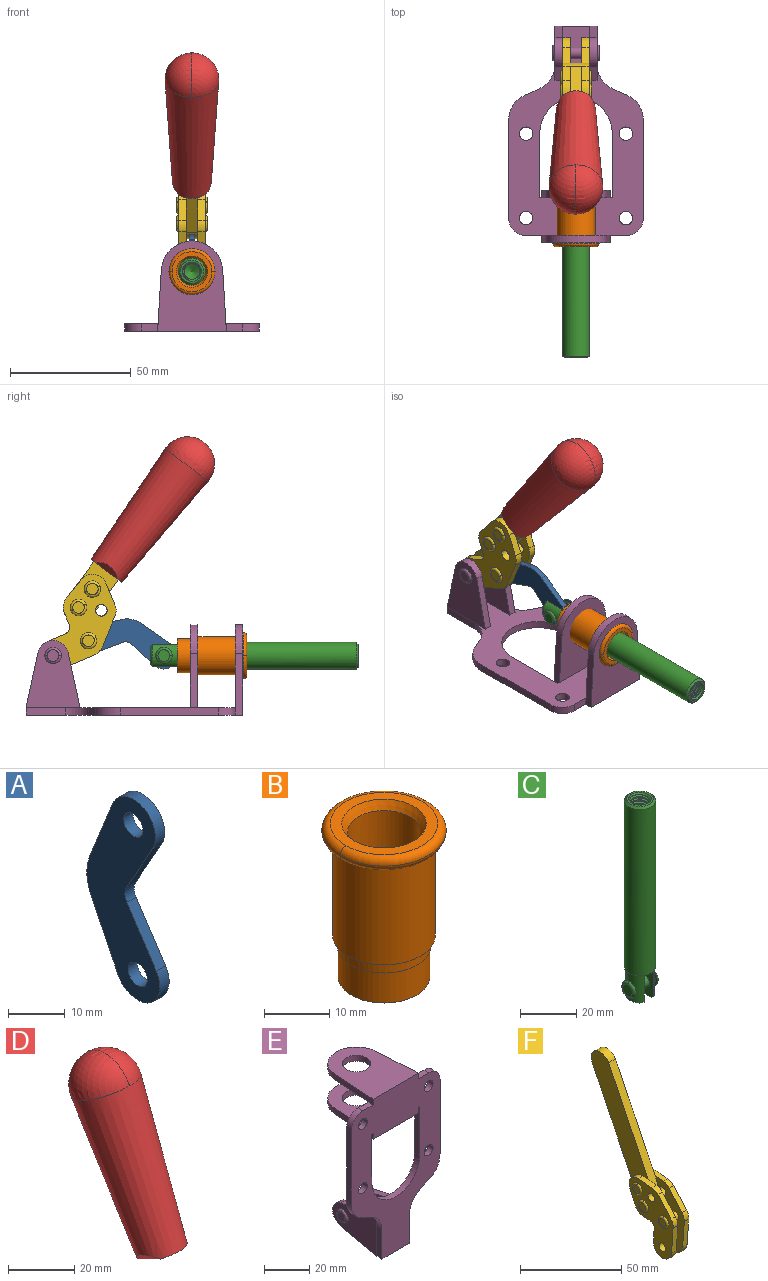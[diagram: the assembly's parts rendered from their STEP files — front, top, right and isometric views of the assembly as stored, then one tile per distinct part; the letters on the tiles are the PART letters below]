
ASSEMBLY  parts=6 mates=6
PART A: 12 faces, bbox 2.3x18.2x42.8 mm
  f0: cylinder r=2.4mm len=4.8mm, axis (1,0,0), area 34.9mm2, adj f4,f11
  f1: cylinder r=10.41mm len=8.47mm, axis (1,0,0), area 20.2mm2, adj f4,f9,f10,f11
  f2: cylinder r=3.05mm len=3.16mm, axis (1,0,0), area 7.7mm2, adj f4,f6,f7,f11
  f3: cylinder r=2.4mm len=4.8mm, axis (1,0,0), area 34.9mm2, adj f4,f11
  f4: plane 42.81x18.23mm, normal (-1,0,0), area 414.1mm2, adj f0,f1,f2,f3,f5,f6,f7,f8
  f5: cylinder r=5.54mm len=10.67mm, axis (1,0,0), area 41.8mm2, adj f4,f6,f10,f11
  f6: plane 11.66x6.53mm, normal (0,-0.87,-0.49), area 30.9mm2, adj f2,f4,f5,f11
  f7: plane 11.17x7.33mm, normal (0,-0.84,0.55), area 30.9mm2, adj f2,f4,f8,f11
  f8: cylinder r=5.54mm len=10.51mm, axis (1,0,0), area 41.8mm2, adj f4,f7,f9,f11
  f9: plane 13.67x6.67mm, normal (0,0.9,-0.44), area 35.1mm2, adj f1,f4,f8,f11
  f10: plane 14.1x5.7mm, normal (0,0.93,0.37), area 35.1mm2, adj f1,f4,f5,f11
  f11: plane 42.81x18.23mm, normal (1,0,0), area 414.1mm2, adj f0,f1,f2,f3,f5,f6,f7,f8
PART B: 15 faces, bbox 20.6x20.6x28.7 mm
  f0: torus R=8.26mm, axis (0,0,1), area 56.8mm2, adj f1,f10,f12
  f1: torus R=8.26mm, axis (0,0,1), area 56.8mm2, adj f0,f6,f13
  f2: cylinder r=5.59mm len=25.91mm, axis (0,0,1), area 909.6mm2, adj f3,f4
  f3: cone r=6.86mm half-angle=45deg, axis (0,0,-1), area 70.2mm2, adj f2,f14
  f4: cone r=6.47mm half-angle=30deg, axis (0,0,1), area 66.7mm2, adj f2,f13
  f5: cylinder r=7.04mm len=14.07mm, axis (0,0,1), area 252.6mm2, adj f11,f14
  f6: torus R=8.26mm, axis (0,0,1), area 56.8mm2, adj f1,f12,f13
  f7: cylinder r=7.16mm len=14.33mm, axis (0,0,1), area 91.5mm2, adj f9,f11
  f8: cylinder r=7.86mm len=18.42mm, axis (0,0,1), area 909.6mm2, adj f9,f10
  f9: plane 15.72x15.72mm, normal (0,0,-1), area 33mm2, adj f7,f8
  f10: plane 16.51x16.51mm, normal (0,0,-1), area 19.9mm2, adj f0,f8,f12
  f11: plane 14.33x14.33mm, normal (0,0,-1), area 5.7mm2, adj f5,f7
  f12: torus R=8.26mm, axis (0,0,1), area 56.8mm2, adj f0,f6,f10
  f13: plane 16.51x16.51mm, normal (0,0,1), area 82.7mm2, adj f1,f4,f6
  f14: plane 14.07x14.07mm, normal (0,0,-1), area 7.8mm2, adj f3,f5
PART C: 48 faces, bbox 12.6x11.1x86.1 mm
  f0: torus R=2.41mm, axis (-1,0,0), area 15mm2, adj f30,f32,f34
  f1: torus R=2.41mm, axis (-1,0,0), area 15mm2, adj f29,f31,f33
  f2: cylinder r=5.54mm len=72.39mm, axis (0,0,1), area 2518.5mm2, adj f3,f4,f42,f43
  f3: cone r=5.54mm half-angle=45deg, axis (0,0,1), area 7.6mm2, adj f2,f5,f41
  f4: cone r=5.54mm half-angle=45deg, axis (0,0,-1), area 34.9mm2, adj f2,f39
  f5: cylinder r=5.08mm len=11.48mm, axis (0,0,1), area 108.3mm2, adj f3,f7,f8,f41
  f6: cylinder r=2.41mm len=4.83mm, axis (-1,0,0), area 71.2mm2, adj f40,f41
  f7: cylinder r=2.41mm len=4.83mm, axis (-1,0,0), area 7.6mm2, adj f5,f34
  f8: cone r=5.08mm half-angle=45deg, axis (0,0,1), area 10.6mm2, adj f5,f37,f41
  f9: cone r=3.98mm half-angle=45deg, axis (0,0,1), area 17.6mm2, adj f27,f39,f45,f46,f47
  f10: cylinder r=2.41mm len=4.83mm, axis (-1,0,0), area 7.6mm2, adj f33,f38
  f11: cylinder r=3.2mm len=6.4mm, axis (0,0,1), area 78.4mm2, adj f12,f28,f44,f45,f47
  f12: cylinder r=3.2mm len=6.4mm, axis (0,0,1), area 10.5mm2, adj f11,f13,f45,f47
  f13: cylinder r=3.2mm len=6.4mm, axis (0,0,1), area 10.5mm2, adj f12,f14,f45,f47
  f14: cylinder r=3.2mm len=6.4mm, axis (0,0,1), area 10.5mm2, adj f13,f15,f45,f47
  f15: cylinder r=3.2mm len=6.4mm, axis (0,0,1), area 10.5mm2, adj f14,f16,f45,f47
  f16: cylinder r=3.2mm len=6.4mm, axis (0,0,1), area 10.5mm2, adj f15,f17,f45,f47
  f17: cylinder r=3.2mm len=6.4mm, axis (0,0,1), area 10.5mm2, adj f16,f18,f45,f47
  f18: cylinder r=3.2mm len=6.4mm, axis (0,0,1), area 10.5mm2, adj f17,f19,f45,f47
  f19: cylinder r=3.2mm len=6.4mm, axis (0,0,1), area 10.5mm2, adj f18,f20,f45,f47
  f20: cylinder r=3.2mm len=6.4mm, axis (0,0,1), area 10.5mm2, adj f19,f21,f45,f47
  f21: cylinder r=3.2mm len=6.4mm, axis (0,0,1), area 10.5mm2, adj f20,f22,f45,f47
  f22: cylinder r=3.2mm len=6.4mm, axis (0,0,1), area 10.5mm2, adj f21,f23,f45,f47
  f23: cylinder r=3.2mm len=6.4mm, axis (0,0,1), area 10.5mm2, adj f22,f24,f45,f47
  f24: cylinder r=3.2mm len=6.4mm, axis (0,0,1), area 10.5mm2, adj f23,f25,f45,f47
  f25: cylinder r=3.2mm len=6.4mm, axis (0,0,1), area 10.5mm2, adj f24,f26,f45,f47
  f26: cylinder r=3.2mm len=6.4mm, axis (0,0,1), area 10.5mm2, adj f25,f27,f45,f47
  f27: cylinder r=3.2mm len=6.4mm, axis (0,0,1), area 7.4mm2, adj f9,f26,f45,f47
  f28: cone r=3.2mm half-angle=60deg, axis (0,0,1), area 37.2mm2, adj f11
  f29: plane 4.83x4.83mm, normal (-1,0,0), area 18.3mm2, adj f1,f31
  f30: plane 4.83x4.83mm, normal (1,0,0), area 18.3mm2, adj f0,f32
  f31: torus R=2.41mm, axis (-1,0,0), area 15mm2, adj f1,f29,f33
  f32: torus R=2.41mm, axis (-1,0,0), area 15mm2, adj f0,f30,f34
  f33: plane 6.83x6.83mm, normal (1,0,0), area 18.3mm2, adj f1,f10,f31
  f34: plane 6.83x6.83mm, normal (-1,0,0), area 18.3mm2, adj f0,f7,f32
  f35: cone r=5.08mm half-angle=45deg, axis (0,0,1), area 10.6mm2, adj f36,f38,f40
  f36: plane 7.25x1.97mm, normal (0,0,-1), area 10mm2, adj f35,f40
  f37: plane 7.25x1.97mm, normal (0,0,-1), area 10mm2, adj f8,f41
  f38: cylinder r=5.08mm len=11.48mm, axis (0,0,1), area 108.3mm2, adj f10,f35,f40,f42
  f39: plane 9.55x9.55mm, normal (0,0,1), area 22mm2, adj f4,f9
  f40: plane 12.76x10.09mm, normal (1,0,0), area 95.7mm2, adj f6,f35,f36,f38,f42,f43
  f41: plane 12.76x10.09mm, normal (-1,0,0), area 95.7mm2, adj f3,f5,f6,f8,f37,f43
  f42: cone r=5.54mm half-angle=45deg, axis (0,0,1), area 7.6mm2, adj f2,f38,f40
  f43: plane 11.07x4.7mm, normal (0,0,-1), area 50.4mm2, adj f2,f40,f41
  f44: plane 0.89x0.62mm, normal (-1,0,0), area 0.3mm2, adj f11,f45,f46,f47
  f45: bspline ~24.8x7.63mm, area 266.6mm2, adj f9,f11,f12,f13,f14,f15,f16,f17
  f46: bspline ~24.87x7.63mm, area 73.6mm2, adj f9,f44,f45,f47
  f47: bspline ~24.98x7.63mm, area 272.5mm2, adj f9,f11,f12,f13,f14,f15,f16,f17
PART D: 11 faces, bbox 22.3x42.6x64.5 mm
  f0: sphere r=11.13mm, area 411.4mm2, adj f1,f8
  f1: cone r=11.11mm half-angle=3.3deg, axis (0,0.44,0.9), area 3251.8mm2, adj f0,f7,f8,f9,f10
  f2: cylinder r=6.16mm len=11.7mm, axis (1,0,0), area 89.5mm2, adj f3,f4,f5,f6
  f3: plane 60.23x36.75mm, normal (-1,0,0), area 763.6mm2, adj f2,f4,f6,f10
  f4: plane 51.37x25.05mm, normal (0,0.9,-0.44), area 264.2mm2, adj f2,f3,f5,f10
  f5: plane 60.23x36.75mm, normal (1,0,0), area 763.6mm2, adj f2,f4,f6,f10
  f6: plane 51.37x25.05mm, normal (0,-0.9,0.44), area 264.2mm2, adj f2,f3,f5,f10
  f7: plane 9.95x5.95mm, normal (0.71,-0.31,-0.64), area 25.8mm2, adj f1,f10
  f8: sphere r=11.13mm, area 411.4mm2, adj f0,f1
  f9: plane 9.95x5.95mm, normal (-0.71,-0.31,-0.64), area 25.8mm2, adj f1,f10
  f10: plane 14.27x11.38mm, normal (0,-0.44,-0.9), area 106.7mm2, adj f1,f3,f4,f5,f6,f7,f9
PART E: 55 faces, bbox 55.7x37.4x89.8 mm
  f0: torus R=2.41mm, axis (-1,0,0), area 15mm2, adj f11,f15,f25
  f1: torus R=2.41mm, axis (-1,0,0), area 15mm2, adj f10,f12,f22
  f2: cylinder r=2.78mm len=5.56mm, axis (0,-1,0), area 54.2mm2, adj f30,f54
  f3: cylinder r=14.99mm len=29.97mm, axis (0,-1,0), area 145.9mm2, adj f30,f49,f53,f54
  f4: cylinder r=2.78mm len=5.56mm, axis (0,-1,0), area 54.2mm2, adj f30,f54
  f5: cylinder r=2.78mm len=5.56mm, axis (0,-1,0), area 54.2mm2, adj f30,f54
  f6: cylinder r=2.78mm len=5.56mm, axis (0,-1,0), area 54.2mm2, adj f30,f54
  f7: cylinder r=6.35mm len=12.7mm, axis (0,0,1), area 123.6mm2, adj f27,f51
  f8: cylinder r=6.35mm len=12.7mm, axis (0,0,-1), area 124.7mm2, adj f21,f35
  f9: cylinder r=2.41mm len=11.18mm, axis (-1,0,0), area 169.4mm2, adj f16,f19
  f10: plane 4.83x4.83mm, normal (1,0,0), area 18.3mm2, adj f1,f12
  f11: plane 4.83x4.83mm, normal (-1,0,0), area 18.3mm2, adj f0,f15
  f12: torus R=2.41mm, axis (-1,0,0), area 15mm2, adj f1,f10,f22
  f13: cylinder r=6.35mm len=12.41mm, axis (1,0,0), area 53.4mm2, adj f18,f19,f22,f23
  f14: cylinder r=6.35mm len=12.41mm, axis (-1,0,0), area 53.4mm2, adj f16,f17,f24,f25
  f15: torus R=2.41mm, axis (-1,0,0), area 15mm2, adj f0,f11,f25
  f16: plane 27.86x22.35mm, normal (1,0,0), area 425.4mm2, adj f9,f14,f17,f24,f30
  f17: plane 22.86x4.97mm, normal (0,0.21,0.98), area 72.5mm2, adj f14,f16,f25,f30
  f18: plane 22.86x4.97mm, normal (0,0.21,0.98), area 72.5mm2, adj f13,f19,f22,f30
  f19: plane 27.86x22.35mm, normal (-1,0,0), area 425.4mm2, adj f9,f13,f18,f23,f30
  f20: cylinder r=12.7mm len=25.35mm, axis (0,0,-1), area 119.8mm2, adj f21,f34,f35,f36
  f21: plane 34.21x28.07mm, normal (0,0,-1), area 702.4mm2, adj f8,f20,f30,f34,f36
  f22: plane 27.96x22.45mm, normal (1,0,0), area 407.2mm2, adj f1,f12,f13,f18,f23,f30,f42,f43
  f23: plane 22.86x4.97mm, normal (0,0.21,-0.98), area 72.5mm2, adj f13,f19,f22,f44
  f24: plane 22.86x4.97mm, normal (0,0.21,-0.98), area 72.5mm2, adj f14,f16,f25,f44
  f25: plane 27.86x22.35mm, normal (-1,0,0), area 407.1mm2, adj f0,f14,f15,f17,f24,f30,f45,f46
  f26: plane 3.1x0.95mm, normal (0,0,-1), area 2.7mm2, adj f30,f49,f50,f54
  f27: plane 34.21x28.07mm, normal (0,0,1), area 702.4mm2, adj f7,f28,f30,f50,f52
  f28: cylinder r=12.7mm len=25.35mm, axis (0,0,1), area 118.8mm2, adj f27,f50,f51,f52
  f29: plane 3.1x0.95mm, normal (0,0,-1), area 2.7mm2, adj f30,f52,f53,f54
  f30: plane 86.54x55.63mm, normal (0,1,0), area 2362.9mm2, adj f2,f3,f4,f5,f6,f16,f17,f18
  f31: plane 40.56x3.1mm, normal (-1,0,0), area 125.7mm2, adj f30,f32,f48,f54
  f32: cylinder r=7.11mm len=7.11mm, axis (0,-1,0), area 34.6mm2, adj f30,f31,f33,f54
  f33: plane 6.67x3.1mm, normal (0,0,1), area 20.4mm2, adj f30,f32,f34,f54
  f34: plane 25.39x3.13mm, normal (-1,0.06,0), area 79.5mm2, adj f20,f21,f33,f35,f54
  f35: plane 37.31x28.45mm, normal (0,0,1), area 789.9mm2, adj f8,f20,f34,f36,f54
  f36: plane 25.39x3.13mm, normal (1,0.06,0), area 79.5mm2, adj f20,f21,f35,f37,f54
  f37: plane 6.67x3.1mm, normal (0,0,1), area 20.4mm2, adj f30,f36,f38,f54
  f38: cylinder r=7.11mm len=7.11mm, axis (0,-1,0), area 34.6mm2, adj f30,f37,f39,f54
  f39: plane 40.56x3.1mm, normal (1,0,0), area 125.7mm2, adj f30,f38,f40,f54
  f40: cylinder r=11.18mm len=10.16mm, axis (0,-1,0), area 39.5mm2, adj f30,f39,f41,f54
  f41: plane 6.09x3.1mm, normal (0.42,0,-0.91), area 20.8mm2, adj f30,f40,f42,f54
  f42: cylinder r=11.18mm len=9.41mm, axis (0,-1,0), area 37.2mm2, adj f22,f30,f41,f43,f54
  f43: plane 16.5x3.1mm, normal (1,0,0), area 51.1mm2, adj f22,f42,f44,f54
  f44: plane 17.37x3.1mm, normal (0,0,-1), area 53.8mm2, adj f23,f24,f30,f43,f45,f54
  f45: plane 16.5x3.1mm, normal (-1,0,0), area 51.1mm2, adj f25,f44,f46,f54
  f46: cylinder r=11.18mm len=9.41mm, axis (0,-1,0), area 37.2mm2, adj f25,f30,f45,f47,f54
  f47: plane 6.09x3.1mm, normal (-0.42,0,-0.91), area 20.8mm2, adj f30,f46,f48,f54
  f48: cylinder r=11.18mm len=10.16mm, axis (0,-1,0), area 39.5mm2, adj f30,f31,f47,f54
  f49: plane 26.54x3.1mm, normal (-1,0,0), area 82.3mm2, adj f3,f26,f30,f54
  f50: plane 25.39x3.1mm, normal (1,0.06,0), area 78.8mm2, adj f26,f27,f28,f51,f54
  f51: plane 37.31x28.45mm, normal (0,0,-1), area 789.9mm2, adj f7,f28,f50,f52,f54
  f52: plane 25.39x3.1mm, normal (-1,0.06,0), area 78.8mm2, adj f27,f28,f29,f51,f54
  f53: plane 26.54x3.1mm, normal (1,0,0), area 82.3mm2, adj f3,f29,f30,f54
  f54: plane 89.66x55.63mm, normal (0,-1,0), area 2678.5mm2, adj f2,f3,f4,f5,f6,f26,f29,f31
PART F: 59 faces, bbox 12.9x60.2x99.6 mm
  f0: torus R=2.39mm, axis (-1,0,0), area 14.9mm2, adj f20,f43,f51
  f1: torus R=2.39mm, axis (-1,0,0), area 14.9mm2, adj f19,f42,f51
  f2: torus R=2.39mm, axis (-1,0,0), area 14.9mm2, adj f18,f35,f51
  f3: torus R=2.39mm, axis (-1,0,0), area 14.9mm2, adj f14,f17,f23
  f4: torus R=2.39mm, axis (-1,0,0), area 14.9mm2, adj f13,f16,f23
  f5: torus R=2.39mm, axis (-1,0,0), area 14.9mm2, adj f12,f15,f23
  f6: cylinder r=2.39mm len=4.78mm, axis (1,0,0), area 46.5mm2, adj f48,f50,f51
  f7: cylinder r=2.39mm len=4.78mm, axis (1,0,0), area 46.5mm2, adj f50,f51
  f8: cylinder r=6.35mm len=12.68mm, axis (1,0,0), area 61.8mm2, adj f38,f39,f50,f51
  f9: cylinder r=2.39mm len=4.78mm, axis (-1,0,0), area 70.5mm2, adj f46,f50
  f10: cylinder r=2.39mm len=4.78mm, axis (-1,0,0), area 46.5mm2, adj f23,f45,f46
  f11: cylinder r=2.39mm len=4.78mm, axis (-1,0,0), area 46.5mm2, adj f23,f46
  f12: plane 4.78x4.78mm, normal (1,0,0), area 17.9mm2, adj f5,f15
  f13: plane 4.78x4.78mm, normal (1,0,0), area 17.9mm2, adj f4,f16
  f14: plane 4.78x4.78mm, normal (1,0,0), area 17.9mm2, adj f3,f17
  f15: torus R=2.39mm, axis (-1,0,0), area 14.9mm2, adj f5,f12,f23
  f16: torus R=2.39mm, axis (-1,0,0), area 14.9mm2, adj f4,f13,f23
  f17: torus R=2.39mm, axis (-1,0,0), area 14.9mm2, adj f3,f14,f23
  f18: plane 4.78x4.78mm, normal (-1,0,0), area 17.9mm2, adj f2,f35
  f19: plane 4.78x4.78mm, normal (-1,0,0), area 17.9mm2, adj f1,f42
  f20: plane 4.78x4.78mm, normal (-1,0,0), area 17.9mm2, adj f0,f43
  f21: plane 2.26x0.2mm, normal (1,0,0), area 0.2mm2, adj f31,f44
  f22: plane 2.26x0.2mm, normal (-1,0,0), area 0.2mm2, adj f41,f44
  f23: plane 39.37x30.77mm, normal (1,0,0), area 565.5mm2, adj f3,f4,f5,f10,f11,f15,f16,f17
  f24: cylinder r=6.1mm len=4.15mm, axis (-1,0,0), area 14.7mm2, adj f23,f25,f32,f46
  f25: plane 10.25x9.01mm, normal (0,-0.75,0.66), area 42.3mm2, adj f23,f24,f26,f46
  f26: cylinder r=6.35mm len=4.64mm, axis (-1,0,0), area 15.6mm2, adj f23,f25,f27,f46
  f27: plane 15.84x3.1mm, normal (0,-1,-0.07), area 49.2mm2, adj f23,f26,f28,f46
  f28: cylinder r=6.35mm len=12.68mm, axis (-1,0,0), area 61.8mm2, adj f23,f27,f29,f46
  f29: plane 8.11x3.1mm, normal (0,1,0.07), area 25.2mm2, adj f23,f28,f30,f46
  f30: cylinder r=3.05mm len=3.25mm, axis (-1,0,0), area 14.8mm2, adj f23,f29,f31,f46
  f31: plane 5.99x3.1mm, normal (0,0.07,-1), area 18.6mm2, adj f21,f23,f30,f44,f46
  f32: plane 9.5x3.1mm, normal (0,-0.07,1), area 29.5mm2, adj f23,f24,f33,f46,f47
  f33: cylinder r=6.1mm len=8.63mm, axis (-1,0,0), area 39.1mm2, adj f23,f32,f34,f47
  f34: plane 8.65x3.96mm, normal (0,0.91,-0.42), area 29.5mm2, adj f23,f33,f44,f47
  f35: torus R=2.39mm, axis (-1,0,0), area 14.9mm2, adj f2,f18,f51
  f36: plane 10.25x9.01mm, normal (0,-0.75,0.66), area 42.3mm2, adj f37,f49,f50,f51
  f37: cylinder r=6.35mm len=4.64mm, axis (1,0,0), area 15.6mm2, adj f36,f38,f50,f51
  f38: plane 15.84x3.1mm, normal (0,-1,-0.07), area 49.2mm2, adj f8,f37,f50,f51
  f39: plane 8.11x3.1mm, normal (0,1,0.07), area 25.2mm2, adj f8,f40,f50,f51
  f40: cylinder r=3.05mm len=3.25mm, axis (1,0,0), area 14.8mm2, adj f39,f41,f50,f51
  f41: plane 5.99x3.1mm, normal (0,0.07,-1), area 18.6mm2, adj f22,f40,f44,f50,f51
  f42: torus R=2.39mm, axis (-1,0,0), area 14.9mm2, adj f1,f19,f51
  f43: torus R=2.39mm, axis (-1,0,0), area 14.9mm2, adj f0,f20,f51
  f44: cylinder r=6.35mm len=12.12mm, axis (-1,0,0), area 128.9mm2, adj f21,f22,f23,f31,f34,f41,f46,f47
  f45: plane 2.65x1.35mm, normal (1,0,0), area 1mm2, adj f10,f55
  f46: plane 39.08x20.42mm, normal (-1,0,0), area 412.5mm2, adj f9,f10,f11,f24,f25,f26,f27,f28
  f47: plane 77.62x39.82mm, normal (1,0,0), area 850mm2, adj f32,f33,f34,f44,f53,f54,f55
  f48: plane 2.65x1.35mm, normal (-1,0,0), area 1mm2, adj f6,f55
  f49: cylinder r=6.1mm len=4.15mm, axis (1,0,0), area 14.7mm2, adj f36,f50,f51,f56
  f50: plane 39.08x20.42mm, normal (1,0,0), area 412.5mm2, adj f6,f7,f8,f9,f36,f37,f38,f39
  f51: plane 39.37x30.77mm, normal (-1,0,0), area 565.5mm2, adj f0,f1,f2,f6,f7,f8,f35,f36
  f52: plane 8.65x3.96mm, normal (0,0.91,-0.42), area 29.5mm2, adj f44,f51,f57,f58
  f53: plane 68.49x33.4mm, normal (0,0.9,-0.44), area 358.1mm2, adj f44,f47,f54,f58
  f54: cylinder r=6.35mm len=12.06mm, axis (1,0,0), area 93.7mm2, adj f47,f53,f55,f58
  f55: plane 68.49x33.4mm, normal (0,-0.9,0.44), area 358.1mm2, adj f44,f45,f46,f47,f48,f50,f54,f58
  f56: plane 9.5x3.1mm, normal (0,-0.07,1), area 29.5mm2, adj f49,f50,f51,f57,f58
  f57: cylinder r=6.1mm len=8.63mm, axis (1,0,0), area 39.1mm2, adj f51,f52,f56,f58
  f58: plane 77.62x39.82mm, normal (-1,0,0), area 850mm2, adj f44,f52,f53,f54,f55,f56,f57
PLACE A rot(axis=(0,-0.65,-0.76),180deg) t=(0,15.25,4)mm
PLACE B rot(axis=(1,0,0),90deg) t=(0,10.16,0)mm
PLACE C rot(axis=(1,0,0),90deg) t=(0,10.93,0)mm
PLACE D rot(axis=(1,0,0),63.2deg) t=(-0.04,1.49,17.12)mm
PLACE E rot(axis=(1,0,0),90deg) t=(0,9.14,0)mm fixed
PLACE F rot(axis=(1,0,0),63.2deg) t=(0,1.49,17.12)mm
MATE fastened D.f2 <-> F.f54  axis (1,0,0) through (-2.35,-15.35,105.23)mm
MATE revolute C.f6 <-> A.f3  axis (-1,0,0) through (0,-4.55,24.61)mm
MATE revolute F.f4 <-> A.f5  axis (-1,0,0) through (0,26.6,30.77)mm
MATE fastened B.f2 <-> E.f7  axis (0,-1,0) through (0,-37.25,24.61)mm
MATE revolute E.f0 <-> F.f7  axis (-1,0,0) through (0,41.23,24.61)mm
MATE slider B.f2 <-> C.f2  axis (0,-1,0) through (0,-37.25,24.61)mm
